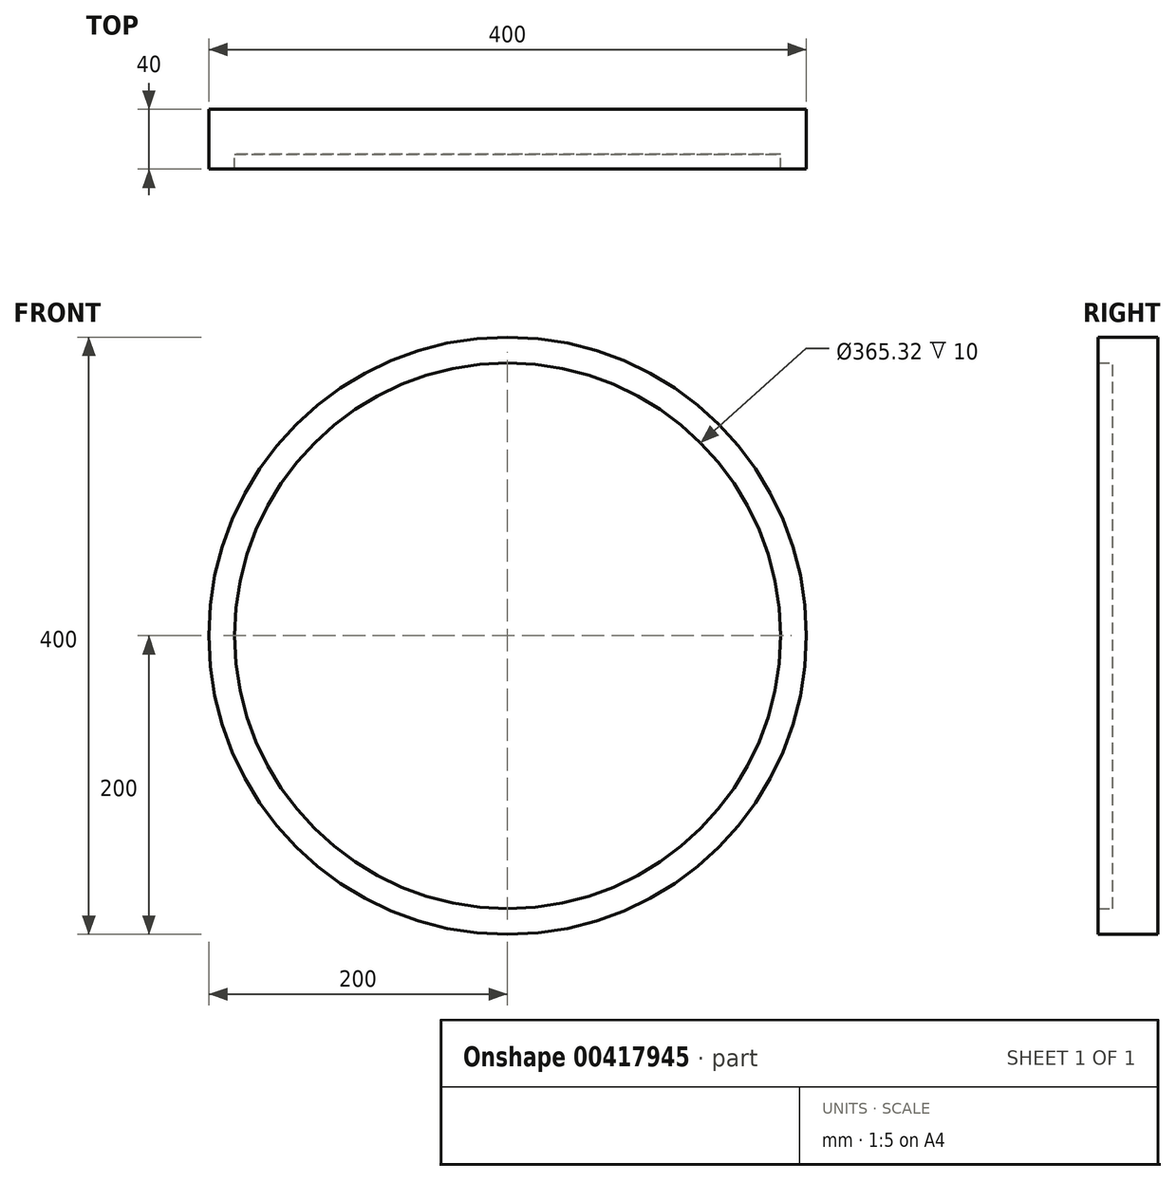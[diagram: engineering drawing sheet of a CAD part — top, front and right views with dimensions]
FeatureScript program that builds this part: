
annotation { "Feature Type Name" : "Feature", "Feature Type Description" : "" }
export const myFeature = defineFeature(function(context is Context, id is Id, definition is map)
    precondition{}
    {
        {
            var Q0;
            Q0=qCreatedBy(makeId("Front.planeOp"),FACE);
            var sketch = newSketch(context, id + "F0", { "sketchPlane" : qUnion([Q0])});
            skCircle(sketch, "E0", {"center": v(0, 0) * mm, "radius": 200 * mm});
            skCircle(sketch, "E1", {"center": v(0, 0) * mm, "radius": 182.66 * mm});
            skSolve(sketch);
        }
        {
            var Q0;
            Q0=makeQuery(id+"F0.imprint","IMPRINT",FACE,{"disambiguationData":[TD([[makeQuery(id+"F0.imprint","IMPRINT",EDGE,{"derivedFrom":sQuery(id+"F0.wireOp",EDGE,"E1")}),1.0]])]});
            var sketch = newSketch(context, id + "F1", { "sketchPlane" : qUnion([Q0])});
            skSolve(sketch);
        }
        {
            var Q0;
            Q0=makeQuery(id+"F0.imprint","IMPRINT",FACE,{"disambiguationData":[TD([[makeQuery(id+"F0.imprint","IMPRINT",EDGE,{"derivedFrom":sQuery(id+"F0.wireOp",EDGE,"E0")}),1.0]])]});
            extrude(context, id + "F2", {"entities" : qUnion([Q0]), "depth" : 40 * mm});
        }
        {
            var Q0;
            Q0=makeQuery(id+"F1.imprint","IMPRINT",FACE,{"disambiguationData":[TD([[makeQuery(id+"F1.imprint","IMPRINT",EDGE,{"derivedFrom":makeQuery(id+"F0.imprint","IMPRINT",EDGE,{"derivedFrom":sQuery(id+"F0.wireOp",EDGE,"E1")})}),1.0]])]});
            extrude(context, id + "F3", {"entities" : qUnion([Q0]), "operationType" : NewBodyOperationType.ADD, "depth" : 30 * mm});
        }
    });
